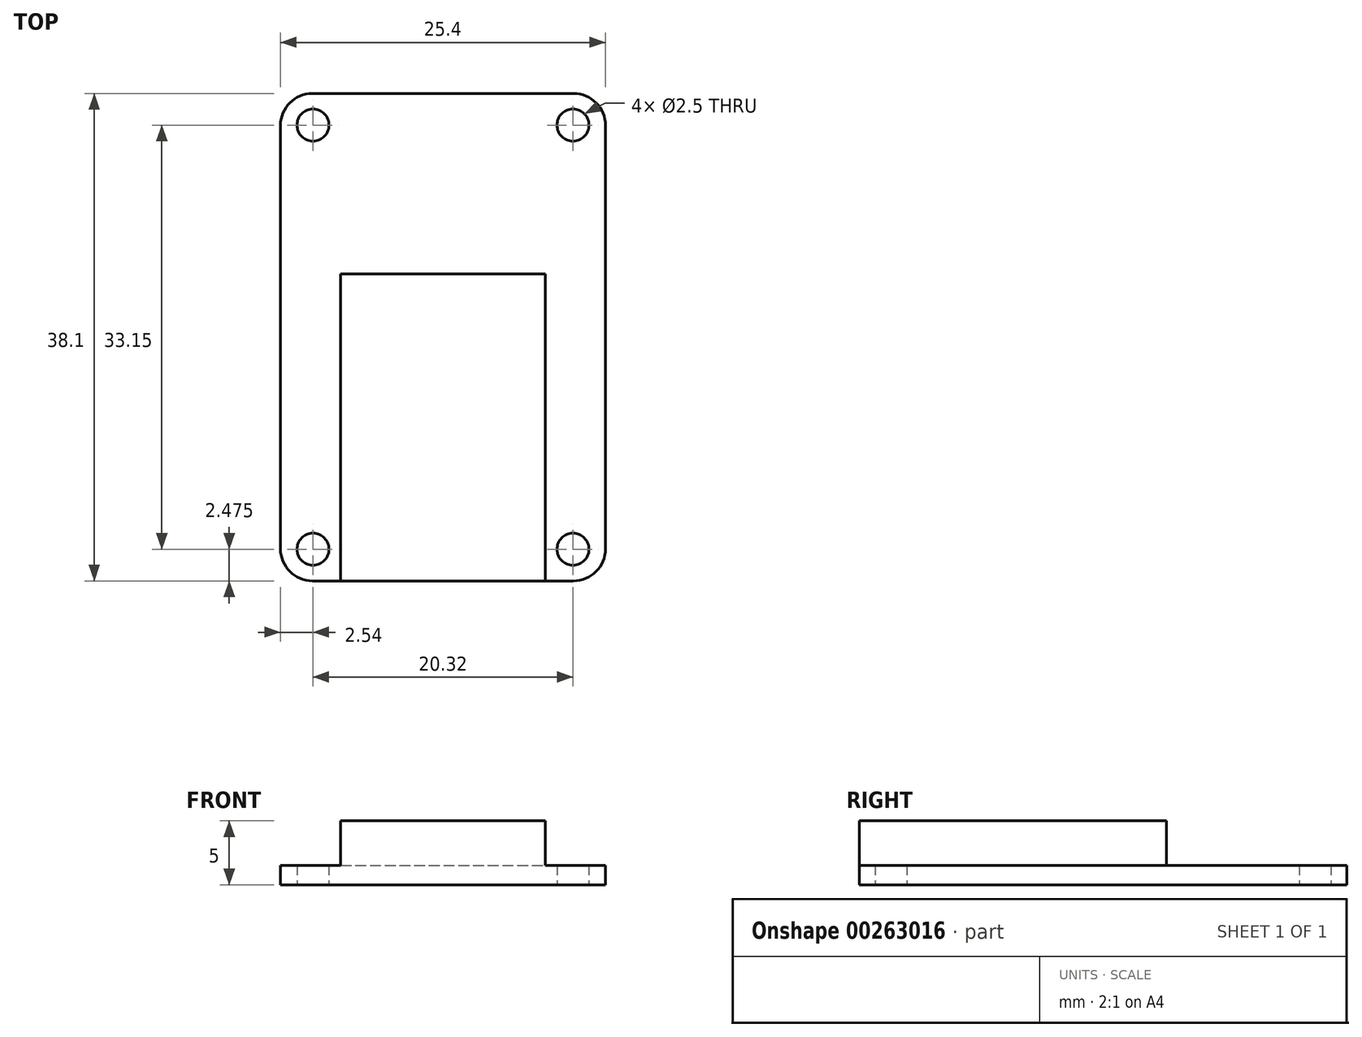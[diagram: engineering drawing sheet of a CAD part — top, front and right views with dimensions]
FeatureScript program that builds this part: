
annotation { "Feature Type Name" : "Feature", "Feature Type Description" : "" }
export const myFeature = defineFeature(function(context is Context, id is Id, definition is map)
    precondition{}
    {
        {
            var Q0;
            Q0=qCreatedBy(makeId("Top.planeOp"),FACE);
            var sketch = newSketch(context, id + "F0", { "sketchPlane" : qUnion([Q0])});
            skLineSegment(sketch, "E0.bottom", {"start": v(2.5, 0) * mm, "end": v(22.9, 0) * mm});
            skLineSegment(sketch, "E0.top", {"start": v(2.5, 38.1) * mm, "end": v(22.9, 38.1) * mm});
            skLineSegment(sketch, "E0.left", {"start": v(0, 2.5) * mm, "end": v(0, 35.6) * mm});
            skLineSegment(sketch, "E0.right", {"start": v(25.4, 2.5) * mm, "end": v(25.4, 35.6) * mm});
            skLineSegment(sketch, "E1", {"start": v(12.7, 38.1) * mm, "end": v(12.7, 0) * mm, "construction": true});
            skLineSegment(sketch, "E2.0", {"start": v(2.54, 38.1) * mm, "end": v(2.54, 0) * mm, "construction": true});
            skLineSegment(sketch, "E3.0", {"start": v(22.86, 38.1) * mm, "end": v(22.86, 0) * mm, "construction": true});
            skLineSegment(sketch, "E4", {"start": v(0, 19.05) * mm, "end": v(25.4, 19.05) * mm, "construction": true});
            skLineSegment(sketch, "E5.0", {"start": v(0, 2.48) * mm, "end": v(25.4, 2.48) * mm, "construction": true});
            skLineSegment(sketch, "E6.0", {"start": v(0, 35.63) * mm, "end": v(25.4, 35.63) * mm, "construction": true});
            skCircle(sketch, "E7", {"center": v(2.54, 2.48) * mm, "radius": 1.25 * mm});
            skCircle(sketch, "E8.MirrorC", {"center": v(22.86, 2.48) * mm, "radius": 1.25 * mm});
            skCircle(sketch, "E9.MirrorC", {"center": v(22.86, 35.62) * mm, "radius": 1.25 * mm});
            skCircle(sketch, "E10.MirrorC", {"center": v(2.54, 35.63) * mm, "radius": 1.25 * mm});
            skPoint(sketch, "E11.visualSharp", {"position": v(25.4, 0) * mm});
            skArc(sketch, "E11.filletArc", {"start": v(22.9, 0) * mm, "mid": v(24.67, 0.73) * mm, "end": v(25.4, 2.5) * mm});
            skPoint(sketch, "E12.visualSharp", {"position": v(0, 0) * mm});
            skArc(sketch, "E12.filletArc", {"start": v(0, 2.5) * mm, "mid": v(0.73, 0.73) * mm, "end": v(2.5, 0) * mm});
            skPoint(sketch, "E13.visualSharp", {"position": v(25.4, 38.1) * mm});
            skArc(sketch, "E13.filletArc", {"start": v(25.4, 35.6) * mm, "mid": v(24.67, 37.37) * mm, "end": v(22.9, 38.1) * mm});
            skPoint(sketch, "E14.visualSharp", {"position": v(0, 38.1) * mm});
            skArc(sketch, "E14.filletArc", {"start": v(2.5, 38.1) * mm, "mid": v(0.73, 37.37) * mm, "end": v(0, 35.6) * mm});
            skSolve(sketch);
        }
        {
            var Q0;
            Q0=makeQuery(id+"F0.imprint","IMPRINT",FACE,{"disambiguationData":[TD([[makeQuery(id+"F0.imprint","IMPRINT",EDGE,{"derivedFrom":sQuery(id+"F0.wireOp",EDGE,"E0.bottom")}),1.0]])]});
            extrude(context, id + "F1", {"entities" : qUnion([Q0]), "depth" : 1.5 * mm});
        }
        {
            var Q0;
            Q0=makeQuery(id+"F1.opExtrude","CAP_FACE",FACE,{"disambiguationData":[OSD([sQuery(id+"F0.wireOp",EDGE,"E0.bottom"),sQuery(id+"F0.wireOp",EDGE,"E0.top"),sQuery(id+"F0.wireOp",EDGE,"E0.left"),sQuery(id+"F0.wireOp",EDGE,"E0.right"),sQuery(id+"F0.wireOp",EDGE,"E7"),sQuery(id+"F0.wireOp",EDGE,"E8.MirrorC"),sQuery(id+"F0.wireOp",EDGE,"E9.MirrorC"),sQuery(id+"F0.wireOp",EDGE,"E10.MirrorC"),sQuery(id+"F0.wireOp",EDGE,"E11.filletArc"),sQuery(id+"F0.wireOp",EDGE,"E12.filletArc"),sQuery(id+"F0.wireOp",EDGE,"E13.filletArc"),sQuery(id+"F0.wireOp",EDGE,"E14.filletArc")])],"isStart":false});
            var sketch = newSketch(context, id + "F2", { "sketchPlane" : qUnion([Q0])});
            skLineSegment(sketch, "E15.bottom", {"start": v(4.7, 0) * mm, "end": v(20.7, 0) * mm});
            skLineSegment(sketch, "E15.top", {"start": v(4.7, 24) * mm, "end": v(20.7, 24) * mm});
            skLineSegment(sketch, "E15.left", {"start": v(4.7, 0) * mm, "end": v(4.7, 24) * mm});
            skLineSegment(sketch, "E15.right", {"start": v(20.7, 0) * mm, "end": v(20.7, 24) * mm});
            skLineSegment(sketch, "E16", {"start": v(12.7, 24) * mm, "end": v(12.7, 0) * mm, "construction": true});
            skSolve(sketch);
        }
        {
            var Q0;
            Q0=makeQuery(id+"F2.imprint","IMPRINT",FACE,{"disambiguationData":[TD([[makeQuery(id+"F2.imprint","IMPRINT",EDGE,{"derivedFrom":sQuery(id+"F2.wireOp",EDGE,"E15.bottom")}),1.0]])]});
            extrude(context, id + "F3", {"entities" : qUnion([Q0]), "operationType" : NewBodyOperationType.ADD, "depth" : 3.5 * mm});
        }
    });
